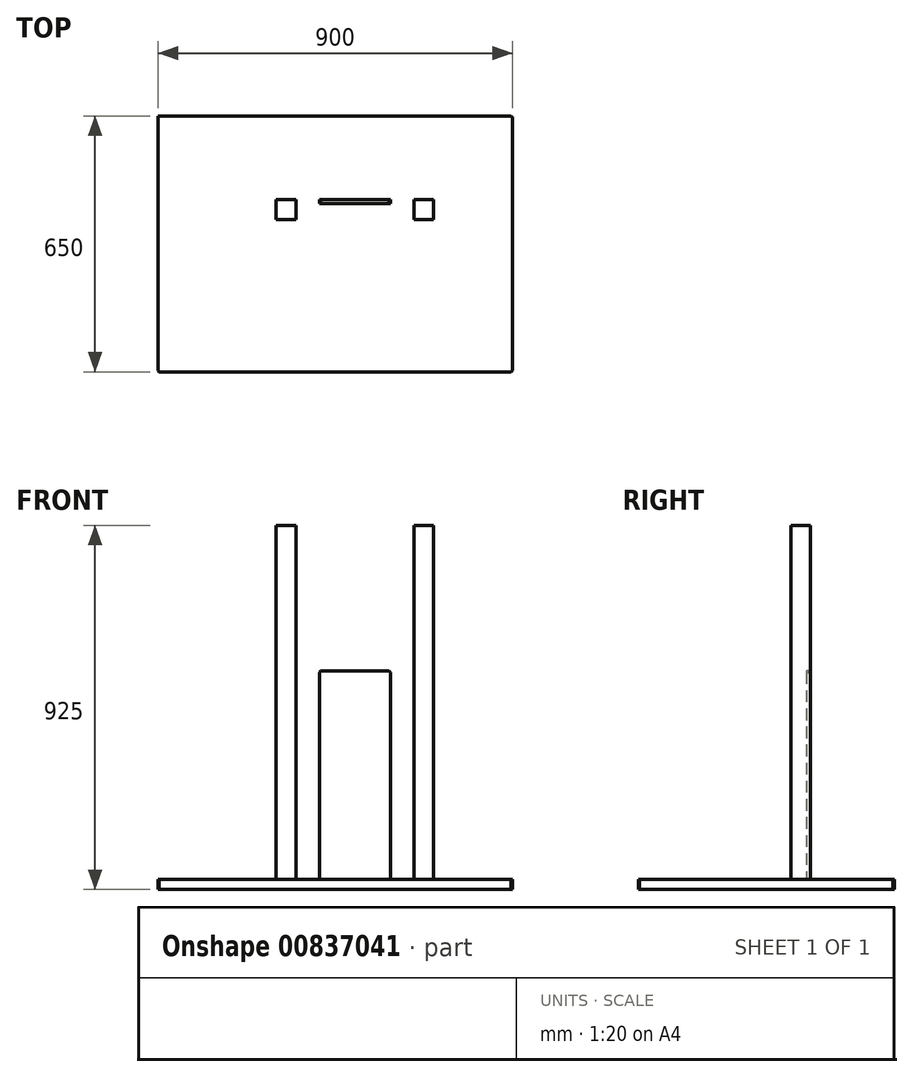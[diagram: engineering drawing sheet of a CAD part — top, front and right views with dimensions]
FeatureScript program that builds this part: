
annotation { "Feature Type Name" : "Feature", "Feature Type Description" : "" }
export const myFeature = defineFeature(function(context is Context, id is Id, definition is map)
    precondition{}
    {
        {
            var Q0;
            Q0=qCreatedBy(makeId("Top.planeOp"),FACE);
            var sketch = newSketch(context, id + "F0", { "sketchPlane" : qUnion([Q0])});
            skLineSegment(sketch, "E0.bottom", {"start": v(3, 0) * mm, "end": v(897, 0) * mm});
            skLineSegment(sketch, "E0.top", {"start": v(0, 650) * mm, "end": v(897, 650) * mm});
            skLineSegment(sketch, "E0.left", {"start": v(0, 3) * mm, "end": v(0, 650) * mm});
            skLineSegment(sketch, "E0.right", {"start": v(900, 3) * mm, "end": v(900, 647) * mm});
            skLineSegment(sketch, "E1", {"start": v(0, 3) * mm, "end": v(3, 0) * mm});
            skLineSegment(sketch, "E2", {"start": v(900, 647) * mm, "end": v(897, 650) * mm});
            skLineSegment(sketch, "E3", {"start": v(897, 0) * mm, "end": v(900, 3) * mm});
            skSolve(sketch);
        }
        {
            var Q0;
            Q0 = qSketchRegion(id + "F0", true);
            extrude(context, id + "F1", {"entities" : qUnion([Q0]), "depth" : 25 * mm, "offsetDistance" : 25 * mm});
        }
        {
            var Q0;
            Q0=makeQuery(id+"F1.opExtrude","CAP_FACE",FACE,{"disambiguationData":[OSD([sQuery(id+"F0.wireOp",EDGE,"E0.bottom"),sQuery(id+"F0.wireOp",EDGE,"E0.top"),sQuery(id+"F0.wireOp",EDGE,"E0.left"),sQuery(id+"F0.wireOp",EDGE,"E0.right"),sQuery(id+"F0.wireOp",EDGE,"E1"),sQuery(id+"F0.wireOp",EDGE,"E2"),sQuery(id+"F0.wireOp",EDGE,"E3")])],"isStart":false});
            var sketch = newSketch(context, id + "F2", { "sketchPlane" : qUnion([Q0])});
            skLineSegment(sketch, "E4.bottom", {"start": v(650, 387.3) * mm, "end": v(700, 387.3) * mm});
            skLineSegment(sketch, "E4.top", {"start": v(650, 437.3) * mm, "end": v(700, 437.3) * mm});
            skLineSegment(sketch, "E4.left", {"start": v(650, 387.3) * mm, "end": v(650, 437.3) * mm});
            skLineSegment(sketch, "E4.right", {"start": v(700, 387.3) * mm, "end": v(700, 437.3) * mm});
            skSolve(sketch);
        }
        {
            var Q0;
            Q0=makeQuery(id+"F2.imprint","IMPRINT",FACE,{"disambiguationData":[TD([[makeQuery(id+"F2.imprint","IMPRINT",EDGE,{"derivedFrom":sQuery(id+"F2.wireOp",EDGE,"E4.bottom")}),1.0]])]});
            extrude(context, id + "F3", {"entities" : qUnion([Q0]), "operationType" : NewBodyOperationType.ADD, "depth" : 900 * mm, "offsetDistance" : 25 * mm});
        }
        {
            var Q0;
            Q0=makeQuery(id+"F1.opExtrude","CAP_FACE",FACE,{"disambiguationData":[OSD([sQuery(id+"F0.wireOp",EDGE,"E0.bottom"),sQuery(id+"F0.wireOp",EDGE,"E0.top"),sQuery(id+"F0.wireOp",EDGE,"E0.left"),sQuery(id+"F0.wireOp",EDGE,"E0.right"),sQuery(id+"F0.wireOp",EDGE,"E1"),sQuery(id+"F0.wireOp",EDGE,"E2"),sQuery(id+"F0.wireOp",EDGE,"E3")])],"isStart":false});
            var sketch = newSketch(context, id + "F4", { "sketchPlane" : qUnion([Q0])});
            skLineSegment(sketch, "E5.bottom", {"start": v(300, 387.3) * mm, "end": v(350, 387.3) * mm});
            skLineSegment(sketch, "E5.top", {"start": v(300, 437.3) * mm, "end": v(350, 437.3) * mm});
            skLineSegment(sketch, "E5.left", {"start": v(300, 387.3) * mm, "end": v(300, 437.3) * mm});
            skLineSegment(sketch, "E5.right", {"start": v(350, 387.3) * mm, "end": v(350, 437.3) * mm});
            skSolve(sketch);
        }
        {
            var Q0;
            Q0=makeQuery(id+"F4.imprint","IMPRINT",FACE,{"disambiguationData":[TD([[makeQuery(id+"F4.imprint","IMPRINT",EDGE,{"derivedFrom":sQuery(id+"F4.wireOp",EDGE,"E5.bottom")}),1.0]])]});
            extrude(context, id + "F5", {"entities" : qUnion([Q0]), "operationType" : NewBodyOperationType.ADD, "depth" : 900 * mm, "offsetDistance" : 25 * mm});
        }
        {
            var Q0;
            Q0=makeQuery(id+"F1.opExtrude","CAP_FACE",FACE,{"disambiguationData":[OSD([sQuery(id+"F0.wireOp",EDGE,"E0.bottom"),sQuery(id+"F0.wireOp",EDGE,"E0.top"),sQuery(id+"F0.wireOp",EDGE,"E0.left"),sQuery(id+"F0.wireOp",EDGE,"E0.right"),sQuery(id+"F0.wireOp",EDGE,"E1"),sQuery(id+"F0.wireOp",EDGE,"E2"),sQuery(id+"F0.wireOp",EDGE,"E3")])],"isStart":false});
            var sketch = newSketch(context, id + "F6", { "sketchPlane" : qUnion([Q0])});
            skLineSegment(sketch, "E6.bottom", {"start": v(410, 437.3) * mm, "end": v(590, 437.3) * mm});
            skLineSegment(sketch, "E6.top", {"start": v(410, 427.3) * mm, "end": v(590, 427.3) * mm});
            skLineSegment(sketch, "E6.left", {"start": v(410, 437.3) * mm, "end": v(410, 427.3) * mm});
            skLineSegment(sketch, "E6.right", {"start": v(590, 437.3) * mm, "end": v(590, 427.3) * mm});
            skSolve(sketch);
        }
        {
            var Q0;
            Q0 = qSketchRegion(id + "F6", true);
            extrude(context, id + "F7", {"entities" : qUnion([Q0]), "operationType" : NewBodyOperationType.ADD, "depth" : 530 * mm, "offsetDistance" : 25 * mm});
        }
        {
            var Q0;
            Q0=makeQuery(id+"F7.opExtrude","SWEPT_FACE",FACE,{"disambiguationData":[OSD([sQuery(id+"F6.wireOp",EDGE,"E6.top")])]});
            var sketch = newSketch(context, id + "F8", { "sketchPlane" : qUnion([Q0])});
            skSolve(sketch);
        }
        {
            var Q0;
            {var subQ0=sQuery(id+"F6.wireOp",EDGE,"E6.top");Q0=makeQuery(id+"F8.imprint","IMPRINT",FACE,{"disambiguationData":[TD([[makeQuery(id+"F8.imprint","IMPRINT",EDGE,{"derivedFrom":makeQuery(id+"F7.opExtrude","CAP_EDGE",EDGE,{"disambiguationData":[OSD([subQ0])],"isStart":false})}),-1.0]])]});}
            var sketch = newSketch(context, id + "F9", { "sketchPlane" : qUnion([Q0])});
            skLineSegment(sketch, "E7", {"start": v(410, 552) * mm, "end": v(413, 555) * mm});
            skLineSegment(sketch, "E8", {"start": v(413, 555) * mm, "end": v(410, 555) * mm});
            skLineSegment(sketch, "E9", {"start": v(410, 555) * mm, "end": v(410, 552) * mm});
            skSolve(sketch);
        }
        {
            var Q0;
            Q0 = qSketchRegion(id + "F9", true);
            extrude(context, id + "F10", {"entities" : qUnion([Q0]), "operationType" : NewBodyOperationType.ADD, "endBound" : BoundingType.UP_TO_NEXT, "oppositeDirection" : true, "depth" : 25 * mm, "offsetDistance" : 25 * mm});
        }
        {
            var Q0;
            Q0=makeQuery(id+"F7.opExtrude","CAP_EDGE",EDGE,{"disambiguationData":[OSD([sQuery(id+"F6.wireOp",EDGE,"E6.left")])],"isStart":false});
            var Q1;
            Q1=makeQuery(id+"F7.opExtrude","CAP_EDGE",EDGE,{"disambiguationData":[OSD([sQuery(id+"F6.wireOp",EDGE,"E6.right")])],"isStart":false});
            chamfer(context, id + "F11", {"entities" : qUnion([Q0, Q1]), "width" : 3 * mm, "tangentPropagation" : true});
        }
    });
